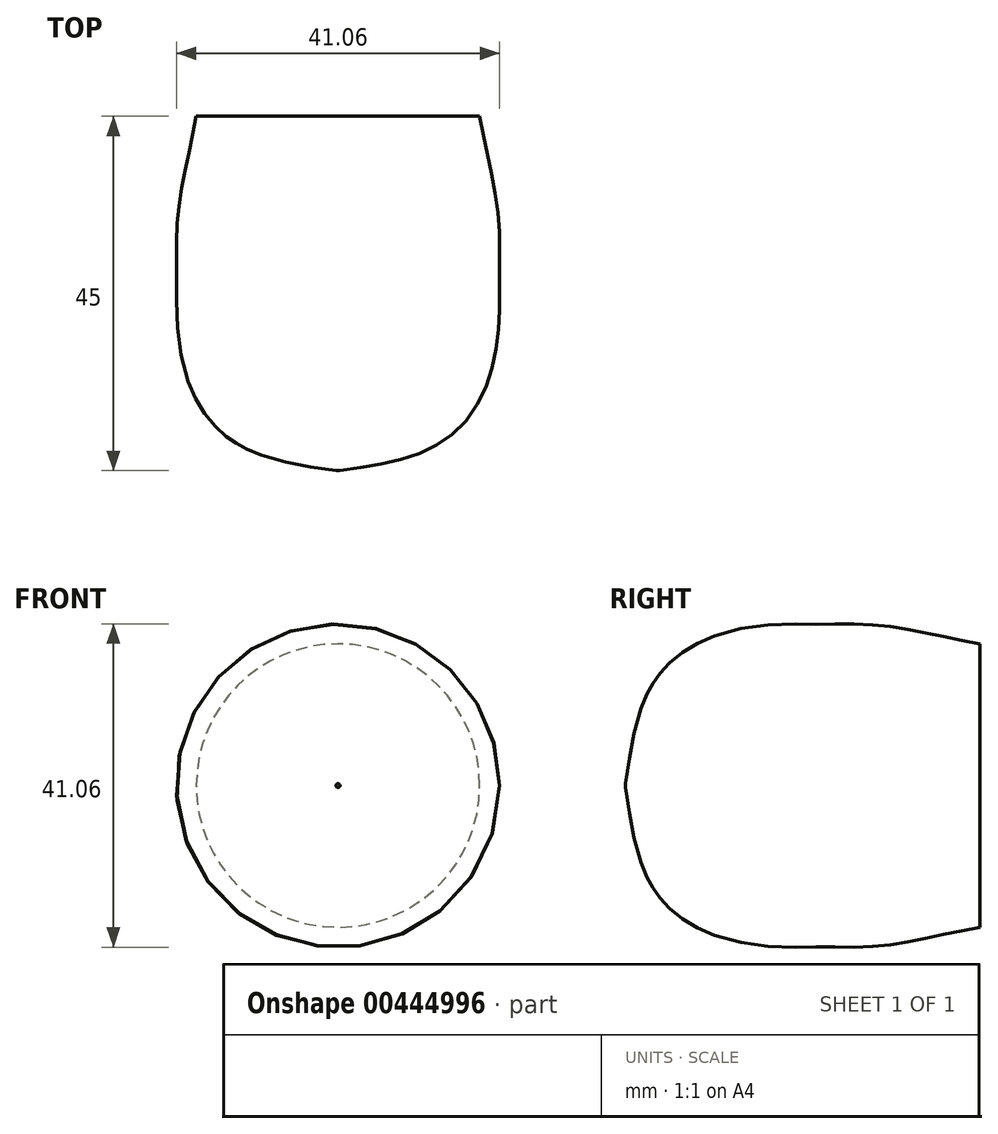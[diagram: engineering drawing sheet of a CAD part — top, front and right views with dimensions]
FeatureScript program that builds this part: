
annotation { "Feature Type Name" : "Feature", "Feature Type Description" : "" }
export const myFeature = defineFeature(function(context is Context, id is Id, definition is map)
    precondition{}
    {
        {
            var Q0;
            Q0=qCreatedBy(makeId("Front.planeOp"),FACE);
            cPlane(context, id + "F0", {"entities" : qUnion([Q0]), "cplaneType" : CPlaneType.OFFSET, "offset" : 5 * mm, "width" : 150 * mm, "height" : 150 * mm});
        }
        {
            var Q0;
            Q0=qCreatedBy(id+"F0.planeOp",FACE);
            cPlane(context, id + "F1", {"entities" : qUnion([Q0]), "cplaneType" : CPlaneType.OFFSET, "offset" : 5 * mm, "width" : 150 * mm, "height" : 150 * mm});
        }
        {
            var Q0;
            Q0=qCreatedBy(id+"F1.planeOp",FACE);
            cPlane(context, id + "F2", {"entities" : qUnion([Q0]), "cplaneType" : CPlaneType.OFFSET, "offset" : 5 * mm, "width" : 150 * mm, "height" : 150 * mm});
        }
        {
            var Q0;
            Q0=qCreatedBy(makeId("Front.planeOp"),FACE);
            var sketch = newSketch(context, id + "F3", { "sketchPlane" : qUnion([Q0])});
            skCircle(sketch, "E0", {"center": v(0, 0) * mm, "radius": 18 * mm});
            skSolve(sketch);
        }
        {
            var Q0;
            Q0=qCreatedBy(id+"F0.planeOp",FACE);
            var sketch = newSketch(context, id + "F4", { "sketchPlane" : qUnion([Q0])});
            skCircle(sketch, "E1", {"center": v(0, 0) * mm, "radius": 19 * mm});
            skSolve(sketch);
        }
        {
            var Q0;
            Q0=qCreatedBy(id+"F1.planeOp",FACE);
            var sketch = newSketch(context, id + "F5", { "sketchPlane" : qUnion([Q0])});
            skCircle(sketch, "E2", {"center": v(0, 0) * mm, "radius": 20 * mm});
            skSolve(sketch);
        }
        {
            var Q0;
            Q0=qCreatedBy(id+"F2.planeOp",FACE);
            cPlane(context, id + "F6", {"entities" : qUnion([Q0]), "cplaneType" : CPlaneType.OFFSET, "offset" : 5 * mm, "width" : 150 * mm, "height" : 150 * mm});
        }
        {
            var Q0;
            Q0=qCreatedBy(id+"F6.planeOp",FACE);
            cPlane(context, id + "F7", {"entities" : qUnion([Q0]), "cplaneType" : CPlaneType.OFFSET, "offset" : 5 * mm, "width" : 150 * mm, "height" : 150 * mm});
        }
        {
            var Q0;
            Q0=qCreatedBy(id+"F7.planeOp",FACE);
            cPlane(context, id + "F8", {"entities" : qUnion([Q0]), "cplaneType" : CPlaneType.OFFSET, "offset" : 5 * mm, "width" : 150 * mm, "height" : 150 * mm});
        }
        {
            var Q0;
            Q0=qCreatedBy(id+"F2.planeOp",FACE);
            var sketch = newSketch(context, id + "F9", { "sketchPlane" : qUnion([Q0])});
            skCircle(sketch, "E3", {"center": v(0, 0) * mm, "radius": 20.5 * mm});
            skSolve(sketch);
        }
        {
            var Q0;
            Q0=qCreatedBy(id+"F6.planeOp",FACE);
            var sketch = newSketch(context, id + "F10", { "sketchPlane" : qUnion([Q0])});
            skCircle(sketch, "E4", {"center": v(0, 0) * mm, "radius": 20.5 * mm});
            skSolve(sketch);
        }
        {
            var Q0;
            Q0=qCreatedBy(id+"F7.planeOp",FACE);
            var sketch = newSketch(context, id + "F11", { "sketchPlane" : qUnion([Q0])});
            skCircle(sketch, "E5", {"center": v(0, 0) * mm, "radius": 20.5 * mm});
            skSolve(sketch);
        }
        {
            var Q0;
            Q0=qCreatedBy(id+"F8.planeOp",FACE);
            cPlane(context, id + "F12", {"entities" : qUnion([Q0]), "cplaneType" : CPlaneType.OFFSET, "offset" : 5 * mm, "width" : 150 * mm, "height" : 150 * mm});
        }
        {
            var Q0;
            Q0=qCreatedBy(id+"F12.planeOp",FACE);
            cPlane(context, id + "F13", {"entities" : qUnion([Q0]), "cplaneType" : CPlaneType.OFFSET, "offset" : 5 * mm, "width" : 150 * mm, "height" : 150 * mm});
        }
        {
            var Q0;
            Q0=qCreatedBy(id+"F8.planeOp",FACE);
            var sketch = newSketch(context, id + "F14", { "sketchPlane" : qUnion([Q0])});
            skCircle(sketch, "E6", {"center": v(0, 0) * mm, "radius": 20 * mm});
            skSolve(sketch);
        }
        {
            var Q0;
            Q0=qCreatedBy(id+"F12.planeOp",FACE);
            var sketch = newSketch(context, id + "F15", { "sketchPlane" : qUnion([Q0])});
            skCircle(sketch, "E7", {"center": v(0, 0) * mm, "radius": 18.5 * mm});
            skSolve(sketch);
        }
        {
            var Q0;
            Q0=qCreatedBy(id+"F13.planeOp",FACE);
            var sketch = newSketch(context, id + "F16", { "sketchPlane" : qUnion([Q0])});
            skCircle(sketch, "E8", {"center": v(0, 0) * mm, "radius": 15 * mm});
            skSolve(sketch);
        }
        {
            var Q0;
            Q0=qCreatedBy(id+"F13.planeOp",FACE);
            cPlane(context, id + "F17", {"entities" : qUnion([Q0]), "cplaneType" : CPlaneType.OFFSET, "offset" : 5 * mm, "width" : 150 * mm, "height" : 150 * mm});
        }
        {
            var Q0;
            Q0=qCreatedBy(id+"F17.planeOp",FACE);
            var sketch = newSketch(context, id + "F18", { "sketchPlane" : qUnion([Q0])});
            skCircle(sketch, "E9", {"center": v(0, 0) * mm, "radius": 0.25 * mm});
            skSolve(sketch);
        }
        {
            var Q0;
            Q0 = qSketchRegion(id + "F3", true);
            var Q1;
            Q1 = qSketchRegion(id + "F4", true);
            var Q2;
            Q2 = qSketchRegion(id + "F5", true);
            var Q3;
            Q3 = qSketchRegion(id + "F9", true);
            var Q4;
            Q4 = qSketchRegion(id + "F10", true);
            var Q5;
            Q5 = qSketchRegion(id + "F11", true);
            var Q6;
            Q6 = qSketchRegion(id + "F14", true);
            var Q7;
            Q7 = qSketchRegion(id + "F15", true);
            var Q8;
            Q8 = qSketchRegion(id + "F16", true);
            var Q9;
            Q9 = qSketchRegion(id + "F18", true);
            var Q10;
            Q10=sQuery(id+"F3.wireOp",EDGE,"E0");
            var Q11;
            Q11=sQuery(id+"F4.wireOp",EDGE,"E1");
            var Q12;
            Q12=sQuery(id+"F5.wireOp",EDGE,"E2");
            var Q13;
            Q13=sQuery(id+"F9.wireOp",EDGE,"E3");
            var Q14;
            Q14=sQuery(id+"F10.wireOp",EDGE,"E4");
            var Q15;
            Q15=sQuery(id+"F11.wireOp",EDGE,"E5");
            var Q16;
            Q16=sQuery(id+"F14.wireOp",EDGE,"E6");
            var Q17;
            Q17=sQuery(id+"F15.wireOp",EDGE,"E7");
            var Q18;
            Q18=sQuery(id+"F16.wireOp",EDGE,"E8");
            var Q19;
            Q19=sQuery(id+"F18.wireOp",EDGE,"E9");
            loft(context, id + "F19", {"bodyType" : ToolBodyType.SURFACE, "sheetProfilesArray" : [{ "sheetProfileEntities" : qUnion([Q0]) }, { "sheetProfileEntities" : qUnion([Q1]) }, { "sheetProfileEntities" : qUnion([Q2]) }, { "sheetProfileEntities" : qUnion([Q3]) }, { "sheetProfileEntities" : qUnion([Q4]) }, { "sheetProfileEntities" : qUnion([Q5]) }, { "sheetProfileEntities" : qUnion([Q6]) }, { "sheetProfileEntities" : qUnion([Q7]) }, { "sheetProfileEntities" : qUnion([Q8]) }, { "sheetProfileEntities" : qUnion([Q9]) }], "wireProfilesArray" : [{ "wireProfileEntities" : qUnion([Q10]) }, { "wireProfileEntities" : qUnion([Q11]) }, { "wireProfileEntities" : qUnion([Q12]) }, { "wireProfileEntities" : qUnion([Q13]) }, { "wireProfileEntities" : qUnion([Q14]) }, { "wireProfileEntities" : qUnion([Q15]) }, { "wireProfileEntities" : qUnion([Q16]) }, { "wireProfileEntities" : qUnion([Q17]) }, { "wireProfileEntities" : qUnion([Q18]) }, { "wireProfileEntities" : qUnion([Q19]) }]});
        }
    });
